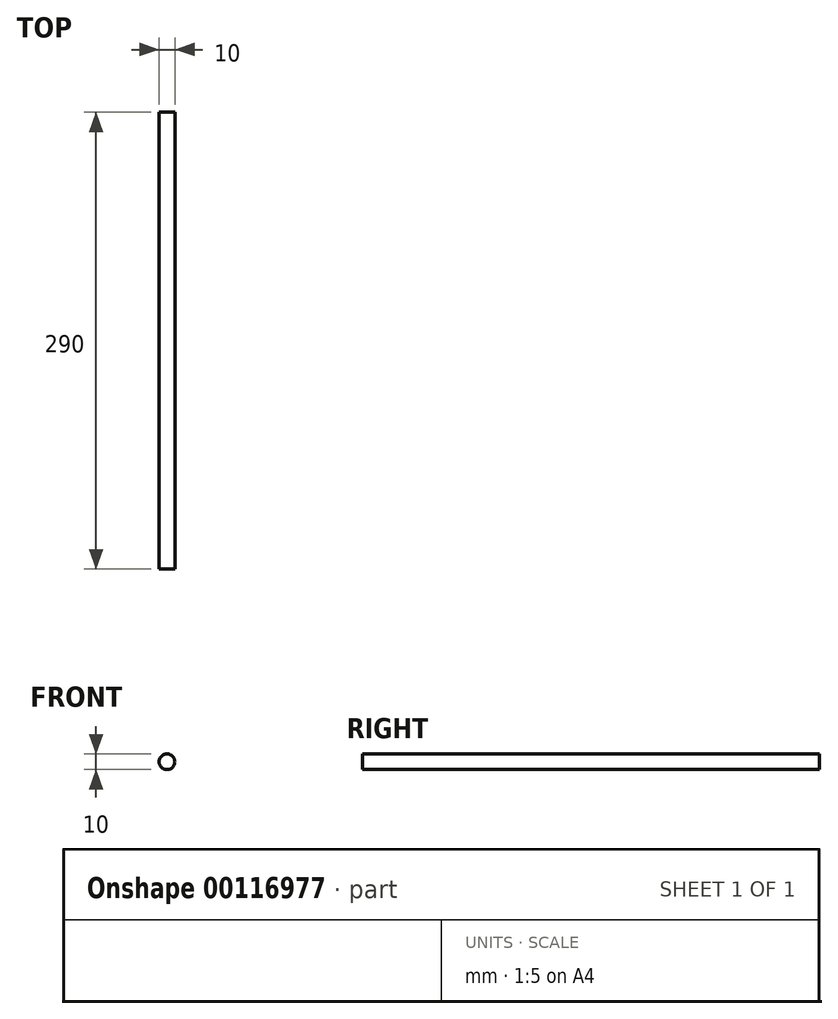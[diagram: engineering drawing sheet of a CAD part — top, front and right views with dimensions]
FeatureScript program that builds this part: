
annotation { "Feature Type Name" : "Feature", "Feature Type Description" : "" }
export const myFeature = defineFeature(function(context is Context, id is Id, definition is map)
    precondition{}
    {
        {
            var Q0;
            Q0=qCreatedBy(makeId("Front.planeOp"),FACE);
            var sketch = newSketch(context, id + "F0", { "sketchPlane" : qUnion([Q0])});
            skCircle(sketch, "E0", {"center": v(0, 0) * mm, "radius": 5 * mm});
            skSolve(sketch);
        }
        {
            var Q0;
            Q0=makeQuery(id+"F0.imprint","IMPRINT",FACE,{"disambiguationData":[TD([[makeQuery(id+"F0.imprint","IMPRINT",EDGE,{"derivedFrom":sQuery(id+"F0.wireOp",EDGE,"E0")}),1.0]])]});
            extrude(context, id + "F1", {"entities" : qUnion([Q0]), "endBound" : BoundingType.SYMMETRIC, "depth" : 290 * mm});
        }
    });
